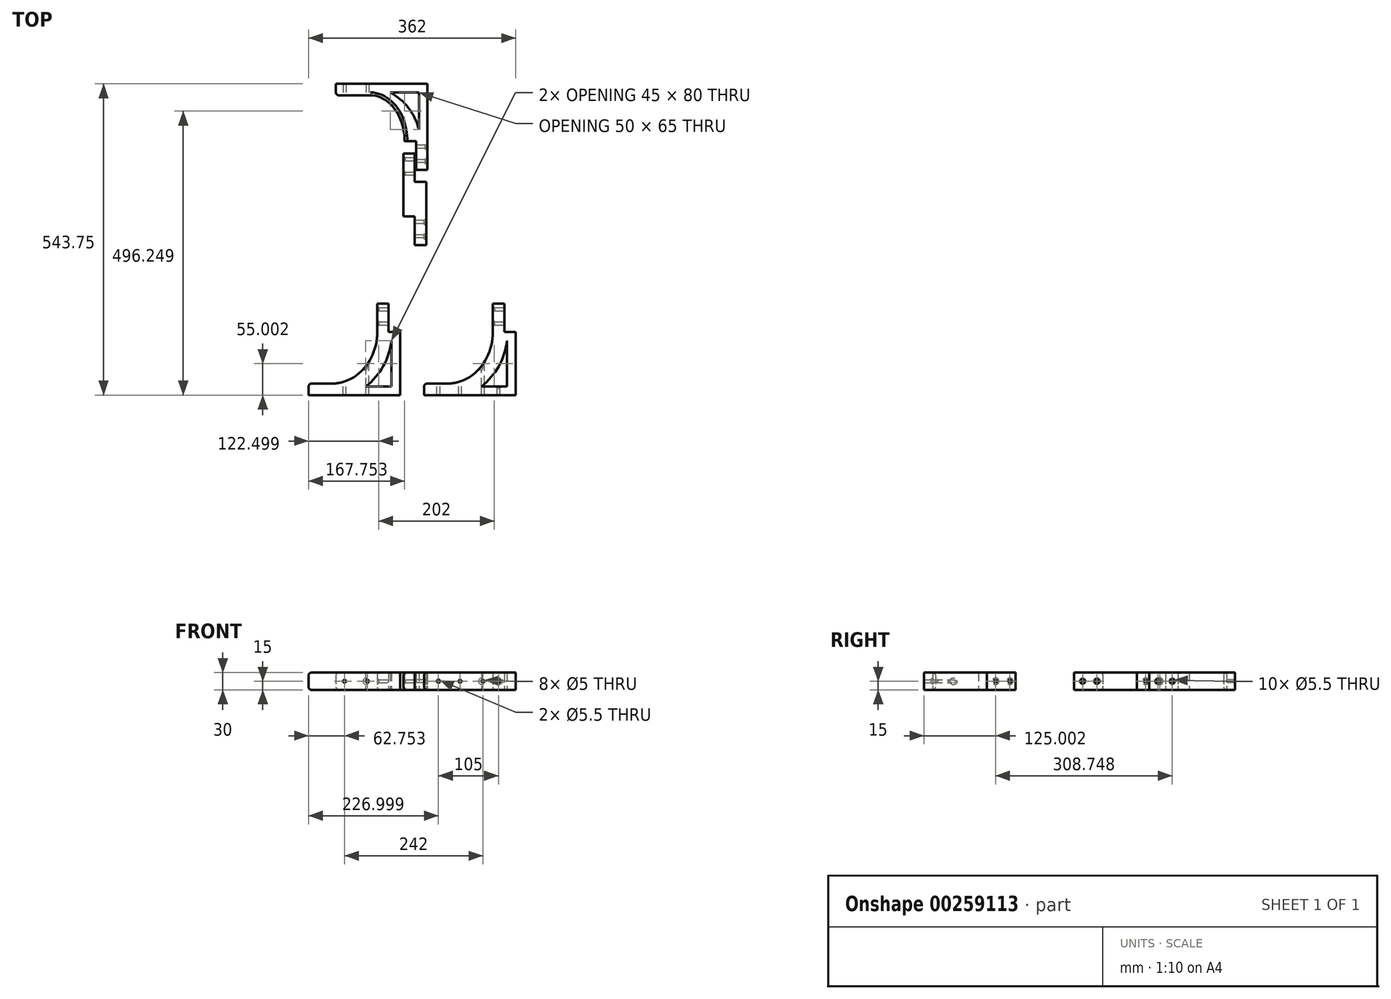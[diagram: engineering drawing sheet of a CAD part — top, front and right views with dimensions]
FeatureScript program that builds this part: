
annotation { "Feature Type Name" : "Feature", "Feature Type Description" : "" }
export const myFeature = defineFeature(function(context is Context, id is Id, definition is map)
    precondition{}
    {
        {
            var Q0;
            Q0=qCreatedBy(makeId("Top.planeOp"),FACE);
            var sketch = newSketch(context, id + "F0", { "sketchPlane" : qUnion([Q0])});
            skLineSegment(sketch, "E0", {"start": v(-102.14, 80.6) * mm, "end": v(57.86, 80.6) * mm});
            skLineSegment(sketch, "E1", {"start": v(57.86, 80.6) * mm, "end": v(57.86, -69.4) * mm});
            skLineSegment(sketch, "E2", {"start": v(57.86, -69.4) * mm, "end": v(37.86, -69.4) * mm});
            skLineSegment(sketch, "E3", {"start": v(17.86, -19.4) * mm, "end": v(17.86, 60.6) * mm});
            skLineSegment(sketch, "E4", {"start": v(17.86, 60.6) * mm, "end": v(-102.14, 60.6) * mm});
            skLineSegment(sketch, "E5", {"start": v(-102.14, 60.6) * mm, "end": v(-102.14, 80.6) * mm});
            skLineSegment(sketch, "E6", {"start": v(37.86, -69.4) * mm, "end": v(37.86, -19.4) * mm});
            skLineSegment(sketch, "E7", {"start": v(37.86, -19.4) * mm, "end": v(17.86, -19.4) * mm});
            skLineSegment(sketch, "E8.MirrorCS", {"start": v(-149.9, -443.15) * mm, "end": v(-149.9, -463.15) * mm});
            skLineSegment(sketch, "E9.MirrorCS", {"start": v(-9.9, -303.15) * mm, "end": v(-9.9, -353.15) * mm});
            skLineSegment(sketch, "E10.MirrorCS", {"start": v(10.1, -463.15) * mm, "end": v(10.1, -353.15) * mm});
            skLineSegment(sketch, "E11.MirrorCS", {"start": v(-149.9, -463.15) * mm, "end": v(10.1, -463.15) * mm});
            skLineSegment(sketch, "E12.MirrorCS", {"start": v(-29.9, -353.15) * mm, "end": v(-29.9, -353.15) * mm});
            skLineSegment(sketch, "E13.MirrorCS", {"start": v(-29.9, -353.15) * mm, "end": v(-109.9, -353.15) * mm, "construction": true});
            skLineSegment(sketch, "E14.MirrorCS", {"start": v(-29.9, -443.15) * mm, "end": v(-149.9, -443.15) * mm});
            skLineSegment(sketch, "E15.MirrorCS", {"start": v(-29.9, -313.15) * mm, "end": v(-29.9, -443.15) * mm});
            skLineSegment(sketch, "E16", {"start": v(-29.9, -313.15) * mm, "end": v(-29.9, -303.15) * mm});
            skLineSegment(sketch, "E17", {"start": v(-9.9, -303.15) * mm, "end": v(-29.9, -303.15) * mm});
            skLineSegment(sketch, "E18", {"start": v(-9.9, -353.15) * mm, "end": v(10.1, -353.15) * mm});
            skLineSegment(sketch, "E19", {"start": v(-109.9, -443.15) * mm, "end": v(-109.9, -353.15) * mm, "construction": true});
            skEllipticalArc(sketch, "E20", {});
            skLineSegment(sketch, "E21", {"start": v(-42.14, 60.6) * mm, "end": v(-42.14, -70.71) * mm, "construction": true});
            skLineSegment(sketch, "E22", {"start": v(17.86, -19.4) * mm, "end": v(-66.1, -19.4) * mm, "construction": true});
            skEllipticalArc(sketch, "E23", {});
            const initialGuessF0  = {"E20": [-0.10989091792114929, -0.3531483935056095, 0, -1, 0.09, 0.08, 0, 1.5707963267948966], "E23": [-0.04213666531701897, -0.019400740689241455, 1, 0, 0.06, 0.08, 6.283185307179586, 1.5707963267948966]};
            skSetInitialGuess(sketch, initialGuessF0);
            skSolve(sketch);
        }
        {
            var Q0;
            Q0 = qSketchRegion(id + "F0", true);
            extrude(context, id + "F1", {"entities" : qUnion([Q0]), "depth" : 30 * mm});
        }
        {
            var Q0;
            Q0=makeQuery(id+"F1.opExtrude","SWEPT_FACE",FACE,{"disambiguationData":[OSD([sQuery(id+"F0.wireOp",EDGE,"E4")])]});
            var sketch = newSketch(context, id + "F2", { "sketchPlane" : qUnion([Q0])});
            skLineSegment(sketch, "E24", {"start": v(-102.14, 15) * mm, "end": v(-102.14, 15) * mm});
            skCircle(sketch, "E25", {"center": v(-87.14, 15) * mm, "radius": 2.5 * mm});
            skCircle(sketch, "E26", {"center": v(-47.14, 15) * mm, "radius": 2.5 * mm});
            skSolve(sketch);
        }
        {
            var Q0;
            Q0 = qSketchRegion(id + "F2", true);
            extrude(context, id + "F3", {"entities" : qUnion([Q0]), "operationType" : NewBodyOperationType.REMOVE, "endBound" : BoundingType.THROUGH_ALL, "depth" : 500 * mm});
        }
        {
            var Q0;
            Q0 = qSketchRegion(id + "F2", true);
            var Q1;
            Q1 = qConstructionFilter(qBodyType(qCreatedBy(id + "F2" ,EDGE), BodyType.WIRE), ConstructionObject.NO);
            extrude(context, id + "F4", {"entities" : qUnion([Q0]), "operationType" : NewBodyOperationType.REMOVE, "surfaceEntities" : qUnion([Q1]), "endBound" : BoundingType.THROUGH_ALL, "oppositeDirection" : true, "depth" : 25 * mm});
        }
        {
            var Q0;
            Q0=makeQuery(id+"F1.opExtrude","SWEPT_FACE",FACE,{"disambiguationData":[OSD([sQuery(id+"F0.wireOp",EDGE,"E6")])]});
            var sketch = newSketch(context, id + "F5", { "sketchPlane" : qUnion([Q0])});
            skLineSegment(sketch, "E27", {"start": v(19.4, 15) * mm, "end": v(69.4, 15) * mm, "construction": true});
            skCircle(sketch, "E28", {"center": v(29.4, 15) * mm, "radius": 2.75 * mm});
            skCircle(sketch, "E29", {"center": v(54.4, 15) * mm, "radius": 2.75 * mm});
            skSolve(sketch);
        }
        {
            var Q0;
            Q0 = qSketchRegion(id + "F5", true);
            extrude(context, id + "F6", {"entities" : qUnion([Q0]), "operationType" : NewBodyOperationType.REMOVE, "endBound" : BoundingType.THROUGH_ALL, "oppositeDirection" : true, "depth" : 25 * mm});
        }
        {
            var Q0;
            Q0=makeQuery(id+"F1.opExtrude","SWEPT_FACE",FACE,{"disambiguationData":[OSD([sQuery(id+"F0.wireOp",EDGE,"E9.MirrorCS")])]});
            var sketch = newSketch(context, id + "F7", { "sketchPlane" : qUnion([Q0])});
            skLineSegment(sketch, "E30", {"start": v(-303.15, 15) * mm, "end": v(-353.15, 15) * mm, "construction": true});
            skCircle(sketch, "E31", {"center": v(-313.15, 15) * mm, "radius": 2.75 * mm});
            skCircle(sketch, "E32", {"center": v(-338.15, 15) * mm, "radius": 2.75 * mm});
            skSolve(sketch);
        }
        {
            var Q0;
            Q0 = qSketchRegion(id + "F7", true);
            extrude(context, id + "F8", {"entities" : qUnion([Q0]), "operationType" : NewBodyOperationType.REMOVE, "endBound" : BoundingType.THROUGH_ALL, "oppositeDirection" : true, "depth" : 25 * mm});
        }
        {
            var Q0;
            Q0=makeQuery(id+"F1.opExtrude","SWEPT_FACE",FACE,{"disambiguationData":[OSD([sQuery(id+"F0.wireOp",EDGE,"E15.MirrorCS"),sQuery(id+"F0.wireOp",EDGE,"E16")])]});
            var sketch = newSketch(context, id + "F9", { "sketchPlane" : qUnion([Q0])});
            skSolve(sketch);
        }
        {
            var Q0;
            Q0=makeQuery(id+"F9.imprint","IMPRINT",FACE,{"disambiguationData":[TD([[makeQuery(id+"F9.imprint","IMPRINT",EDGE,{"derivedFrom":makeQuery(id+"F8.boolean.opBoolean","INTERSECT",EDGE,{"derivedFrom":[makeQuery(id+"F1.opExtrude","SWEPT_FACE",FACE,{"disambiguationData":[OSD([sQuery(id+"F0.wireOp",EDGE,"E15.MirrorCS"),sQuery(id+"F0.wireOp",EDGE,"E16")])]}),makeQuery(id+"F8.opExtrude","SWEPT_FACE",FACE,{"disambiguationData":[OSD([sQuery(id+"F7.wireOp",EDGE,"E31")])]})]})}),1.0]])]});
            var Q1;
            Q1=makeQuery(id+"F9.imprint","IMPRINT",FACE,{"disambiguationData":[TD([[makeQuery(id+"F9.imprint","IMPRINT",EDGE,{"derivedFrom":makeQuery(id+"F8.boolean.opBoolean","INTERSECT",EDGE,{"derivedFrom":[makeQuery(id+"F1.opExtrude","SWEPT_FACE",FACE,{"disambiguationData":[OSD([sQuery(id+"F0.wireOp",EDGE,"E15.MirrorCS"),sQuery(id+"F0.wireOp",EDGE,"E16")])]}),makeQuery(id+"F8.opExtrude","SWEPT_FACE",FACE,{"disambiguationData":[OSD([sQuery(id+"F7.wireOp",EDGE,"E32")])]})]})}),1.0]])]});
            var Q2;
            Q2=makeQuery(id+"F9.imprint","IMPRINT",FACE,{"disambiguationData":[TD([[makeQuery(id+"F9.imprint","IMPRINT",EDGE,{"derivedFrom":sQuery(id+"F9.wireOp",EDGE,"272e9433-be63-4afe-911a-4138f05e95d2.0")}),-1.0]])]});
            var Q3;
            Q3=makeQuery(id+"F9.imprint","IMPRINT",FACE,{"disambiguationData":[TD([[makeQuery(id+"F9.imprint","IMPRINT",EDGE,{"derivedFrom":sQuery(id+"F9.wireOp",EDGE,"0a3e6cfc-d7aa-49eb-8218-c1783a06f407.0")}),-1.0]])]});
            extrude(context, id + "F10", {"entities" : qUnion([Q0, Q1, Q2, Q3]), "operationType" : NewBodyOperationType.REMOVE, "oppositeDirection" : true, "depth" : 4.5 * mm});
        }
        {
            var Q0;
            Q0=makeQuery(id+"F1.opExtrude","CAP_FACE",FACE,{"disambiguationData":[OSD([sQuery(id+"F0.wireOp",EDGE,"E8.MirrorCS"),sQuery(id+"F0.wireOp",EDGE,"E9.MirrorCS"),sQuery(id+"F0.wireOp",EDGE,"E10.MirrorCS"),sQuery(id+"F0.wireOp",EDGE,"E11.MirrorCS"),sQuery(id+"F0.wireOp",EDGE,"E14.MirrorCS"),sQuery(id+"F0.wireOp",EDGE,"E15.MirrorCS"),sQuery(id+"F0.wireOp",EDGE,"E16"),sQuery(id+"F0.wireOp",EDGE,"E17"),sQuery(id+"F0.wireOp",EDGE,"E18"),sQuery(id+"F0.wireOp",EDGE,"E20")])],"isStart":true});
            var sketch = newSketch(context, id + "F11", { "sketchPlane" : qUnion([Q0])});
            skLineSegment(sketch, "E33", {"start": v(-49.9, 448.15) * mm, "end": v(-4.9, 448.15) * mm});
            skLineSegment(sketch, "E34", {"start": v(-4.9, 448.15) * mm, "end": v(-4.9, 368.15) * mm});
            skArc(sketch, "E35", {"start": v(-4.9, 368.15) * mm, "mid": v(-19.44, 412.62) * mm, "end": v(-49.9, 448.15) * mm});
            skSolve(sketch);
        }
        {
            var Q0;
            Q0=makeQuery(id+"F11.imprint","IMPRINT",FACE,{"disambiguationData":[TD([[makeQuery(id+"F11.imprint","IMPRINT",EDGE,{"derivedFrom":sQuery(id+"F11.wireOp",EDGE,"E33")}),-1.0]])]});
            extrude(context, id + "F12", {"entities" : qUnion([Q0]), "operationType" : NewBodyOperationType.REMOVE, "endBound" : BoundingType.THROUGH_ALL, "oppositeDirection" : true, "depth" : 25 * mm});
        }
        {
            var Q0;
            Q0=makeQuery(id+"F1.opExtrude","CAP_FACE",FACE,{"disambiguationData":[OSD([sQuery(id+"F0.wireOp",EDGE,"E0"),sQuery(id+"F0.wireOp",EDGE,"E1"),sQuery(id+"F0.wireOp",EDGE,"E2"),sQuery(id+"F0.wireOp",EDGE,"E4"),sQuery(id+"F0.wireOp",EDGE,"E5"),sQuery(id+"F0.wireOp",EDGE,"E6"),sQuery(id+"F0.wireOp",EDGE,"E7"),sQuery(id+"F0.wireOp",EDGE,"E23")])],"isStart":true});
            var sketch = newSketch(context, id + "F13", { "sketchPlane" : qUnion([Q0])});
            skLineSegment(sketch, "E36", {"start": v(-7.14, -65.6) * mm, "end": v(42.86, -65.6) * mm});
            skLineSegment(sketch, "E37", {"start": v(42.86, -65.6) * mm, "end": v(42.86, -0.6) * mm});
            skArc(sketch, "E38", {"start": v(-7.14, -65.6) * mm, "mid": v(24.83, -38.46) * mm, "end": v(42.86, -0.6) * mm});
            skSolve(sketch);
        }
        {
            var Q0;
            Q0=makeQuery(id+"F13.imprint","IMPRINT",FACE,{"disambiguationData":[TD([[makeQuery(id+"F13.imprint","IMPRINT",EDGE,{"derivedFrom":sQuery(id+"F13.wireOp",EDGE,"E36")}),1.0]])]});
            extrude(context, id + "F14", {"entities" : qUnion([Q0]), "operationType" : NewBodyOperationType.REMOVE, "endBound" : BoundingType.THROUGH_ALL, "oppositeDirection" : true, "depth" : 25 * mm});
        }
        {
            var Q0;
            Q0=makeQuery(id+"F3.boolean.opBoolean","INTERSECT",EDGE,{"derivedFrom":[makeQuery(id+"F1.opExtrude","SWEPT_FACE",FACE,{"disambiguationData":[OSD([sQuery(id+"F0.wireOp",EDGE,"E20")])]}),makeQuery(id+"F3.opExtrude","SWEPT_FACE",FACE,{"disambiguationData":[OSD([sQuery(id+"F2.wireOp",EDGE,"E26")])]})]});
            var Q1;
            Q1=makeQuery(id+"F3.boolean.opBoolean","INTERSECT",EDGE,{"derivedFrom":[makeQuery(id+"F1.opExtrude","SWEPT_FACE",FACE,{"disambiguationData":[OSD([sQuery(id+"F0.wireOp",EDGE,"E14.MirrorCS")])]}),makeQuery(id+"F3.opExtrude","SWEPT_FACE",FACE,{"disambiguationData":[OSD([sQuery(id+"F2.wireOp",EDGE,"E25")])]})]});
            var Q2;
            Q2=makeQuery(id+"F3.boolean.opBoolean","INTERSECT",EDGE,{"derivedFrom":[makeQuery(id+"F1.opExtrude","SWEPT_FACE",FACE,{"disambiguationData":[OSD([sQuery(id+"F0.wireOp",EDGE,"E14.MirrorCS")])]}),makeQuery(id+"F3.opExtrude","SWEPT_FACE",FACE,{"disambiguationData":[OSD([sQuery(id+"F2.wireOp",EDGE,"E25")])]})]});
            var Q3;
            Q3=makeQuery(id+"F4.boolean.opBoolean","COPY",EDGE,{"derivedFrom":makeQuery(id+"F4.opExtrude","CAP_EDGE",EDGE,{"disambiguationData":[OSD([sQuery(id+"F2.wireOp",EDGE,"E25")])],"isStart":true})});
            var Q4;
            Q4=makeQuery(id+"F4.boolean.opBoolean","COPY",EDGE,{"derivedFrom":makeQuery(id+"F4.opExtrude","CAP_EDGE",EDGE,{"disambiguationData":[OSD([sQuery(id+"F2.wireOp",EDGE,"E26")])],"isStart":true})});
            chamfer(context, id + "F15", {"entities" : qUnion([Q0, Q1, Q2, Q3, Q4]), "width" : 3 * mm, "tangentPropagation" : true});
        }
        {
            var Q0;
            Q0=makeQuery(id+"F1.opExtrude","CAP_EDGE",EDGE,{"disambiguationData":[OSD([sQuery(id+"F0.wireOp",EDGE,"E14.MirrorCS")])],"isStart":true});
            var Q1;
            Q1=makeQuery(id+"F1.opExtrude","SWEPT_EDGE",EDGE,{"disambiguationData":[OSD([sQuery(id+"F0.wireOp",EDGE,"E8.MirrorCS"),sQuery(id+"F0.wireOp",EDGE,"E14.MirrorCS")])]});
            var Q2;
            Q2=makeQuery(id+"F1.opExtrude","CAP_EDGE",EDGE,{"disambiguationData":[OSD([sQuery(id+"F0.wireOp",EDGE,"E14.MirrorCS")])],"isStart":false});
            var Q3;
            Q3=makeQuery(id+"F1.opExtrude","CAP_EDGE",EDGE,{"disambiguationData":[OSD([sQuery(id+"F0.wireOp",EDGE,"E8.MirrorCS")])],"isStart":true});
            var Q4;
            Q4=makeQuery(id+"F1.opExtrude","CAP_EDGE",EDGE,{"disambiguationData":[OSD([sQuery(id+"F0.wireOp",EDGE,"E8.MirrorCS")])],"isStart":false});
            var Q5;
            Q5=makeQuery(id+"F1.opExtrude","CAP_EDGE",EDGE,{"disambiguationData":[OSD([sQuery(id+"F0.wireOp",EDGE,"E4")])],"isStart":true});
            var Q6;
            Q6=makeQuery(id+"F1.opExtrude","CAP_EDGE",EDGE,{"disambiguationData":[OSD([sQuery(id+"F0.wireOp",EDGE,"E5")])],"isStart":true});
            var Q7;
            Q7=makeQuery(id+"F1.opExtrude","SWEPT_EDGE",EDGE,{"disambiguationData":[OSD([sQuery(id+"F0.wireOp",EDGE,"E4"),sQuery(id+"F0.wireOp",EDGE,"E5")])]});
            var Q8;
            Q8=makeQuery(id+"F1.opExtrude","CAP_EDGE",EDGE,{"disambiguationData":[OSD([sQuery(id+"F0.wireOp",EDGE,"E5")])],"isStart":false});
            var Q9;
            Q9=makeQuery(id+"F1.opExtrude","CAP_EDGE",EDGE,{"disambiguationData":[OSD([sQuery(id+"F0.wireOp",EDGE,"E4")])],"isStart":false});
            fillet(context, id + "F16", {"entities" : qUnion([Q0, Q1, Q2, Q3, Q4, Q5, Q6, Q7, Q8, Q9]), "radius" : 5 * mm, "tangentPropagation" : true, "allowEdgeOverflow" : false});
        }
        {
            var Q0;
            Q0=makeQuery(id+"F8.boolean.opBoolean","INTERSECT",EDGE,{"derivedFrom":[makeQuery(id+"F1.opExtrude","SWEPT_FACE",FACE,{"disambiguationData":[OSD([sQuery(id+"F0.wireOp",EDGE,"E15.MirrorCS"),sQuery(id+"F0.wireOp",EDGE,"E16")])]}),makeQuery(id+"F8.opExtrude","SWEPT_FACE",FACE,{"disambiguationData":[OSD([sQuery(id+"F7.wireOp",EDGE,"E31")])]})]});
            var Q1;
            Q1=makeQuery(id+"F8.boolean.opBoolean","INTERSECT",EDGE,{"derivedFrom":[makeQuery(id+"F1.opExtrude","SWEPT_FACE",FACE,{"disambiguationData":[OSD([sQuery(id+"F0.wireOp",EDGE,"E15.MirrorCS"),sQuery(id+"F0.wireOp",EDGE,"E16")])]}),makeQuery(id+"F8.opExtrude","SWEPT_FACE",FACE,{"disambiguationData":[OSD([sQuery(id+"F7.wireOp",EDGE,"E32")])]})]});
            chamfer(context, id + "F17", {"entities" : qUnion([Q0, Q1]), "width" : 3 * mm, "tangentPropagation" : true});
        }
        {
            var Q0;
            Q0=makeQuery(id+"F1.opExtrude","SWEPT_FACE",FACE,{"disambiguationData":[OSD([sQuery(id+"F0.wireOp",EDGE,"E1")])]});
            var sketch = newSketch(context, id + "F18", { "sketchPlane" : qUnion([Q0])});
            skCircle(sketch, "E39.cCircle", {"center": v(-54.4, 15) * mm, "radius": 4.25 * mm, "construction": true});
            skLineSegment(sketch, "E39.0", {"start": v(-50.15, 17.45) * mm, "end": v(-50.15, 12.55) * mm});
            skLineSegment(sketch, "E39.1", {"start": v(-50.15, 12.55) * mm, "end": v(-54.4, 10.1) * mm});
            skLineSegment(sketch, "E39.2", {"start": v(-54.4, 10.1) * mm, "end": v(-58.65, 12.55) * mm});
            skLineSegment(sketch, "E39.3", {"start": v(-58.65, 12.55) * mm, "end": v(-58.65, 17.45) * mm});
            skLineSegment(sketch, "E39.4", {"start": v(-58.65, 17.45) * mm, "end": v(-54.4, 19.9) * mm});
            skLineSegment(sketch, "E39.5", {"start": v(-54.4, 19.9) * mm, "end": v(-50.15, 17.45) * mm});
            skPoint(sketch, "E39.0.midPoint", {"position": v(-50.15, 15) * mm});
            skCircle(sketch, "E40.cCircle", {"center": v(-29.4, 15) * mm, "radius": 4.25 * mm, "construction": true});
            skLineSegment(sketch, "E40.0", {"start": v(-25.15, 17.45) * mm, "end": v(-25.15, 12.55) * mm});
            skLineSegment(sketch, "E40.1", {"start": v(-25.15, 12.55) * mm, "end": v(-29.4, 10.1) * mm});
            skLineSegment(sketch, "E40.2", {"start": v(-29.4, 10.1) * mm, "end": v(-33.65, 12.55) * mm});
            skLineSegment(sketch, "E40.3", {"start": v(-33.65, 12.55) * mm, "end": v(-33.65, 17.45) * mm});
            skLineSegment(sketch, "E40.4", {"start": v(-33.65, 17.45) * mm, "end": v(-29.4, 19.9) * mm});
            skLineSegment(sketch, "E40.5", {"start": v(-29.4, 19.9) * mm, "end": v(-25.15, 17.45) * mm});
            skPoint(sketch, "E40.0.midPoint", {"position": v(-25.15, 15) * mm});
            skSolve(sketch);
        }
        {
            var Q0;
            Q0=makeQuery(id+"F18.imprint","IMPRINT",FACE,{"disambiguationData":[TD([[makeQuery(id+"F18.imprint","IMPRINT",EDGE,{"derivedFrom":sQuery(id+"F18.wireOp",EDGE,"E39.0")}),-1.0]])]});
            var Q1;
            Q1=makeQuery(id+"F18.imprint","IMPRINT",FACE,{"disambiguationData":[TD([[makeQuery(id+"F18.imprint","IMPRINT",EDGE,{"derivedFrom":sQuery(id+"F18.wireOp",EDGE,"E40.0")}),-1.0]])]});
            extrude(context, id + "F19", {"entities" : qUnion([Q0, Q1]), "operationType" : NewBodyOperationType.REMOVE, "oppositeDirection" : true, "depth" : 4 * mm});
        }
        {
            var Q0;
            Q0=qCreatedBy(makeId("Top.planeOp"),FACE);
            var sketch = newSketch(context, id + "F20", { "sketchPlane" : qUnion([Q0])});
            skLineSegment(sketch, "E41", {"start": v(15.8, -40.83) * mm, "end": v(15.8, -150.92) * mm});
            skLineSegment(sketch, "E42", {"start": v(15.8, -150.92) * mm, "end": v(35.8, -150.92) * mm});
            skLineSegment(sketch, "E43", {"start": v(35.8, -150.92) * mm, "end": v(35.8, -200.92) * mm});
            skLineSegment(sketch, "E44", {"start": v(35.8, -200.92) * mm, "end": v(55.8, -200.92) * mm});
            skLineSegment(sketch, "E45", {"start": v(55.8, -200.92) * mm, "end": v(55.8, -90.92) * mm});
            skLineSegment(sketch, "E46", {"start": v(55.8, -90.92) * mm, "end": v(35.8, -90.92) * mm});
            skLineSegment(sketch, "E47", {"start": v(35.8, -90.92) * mm, "end": v(35.8, -40.92) * mm});
            skLineSegment(sketch, "E48", {"start": v(35.8, -40.92) * mm, "end": v(15.8, -40.83) * mm});
            skSolve(sketch);
        }
        {
            var Q0;
            Q0 = qSketchRegion(id + "F20", true);
            extrude(context, id + "F21", {"entities" : qUnion([Q0]), "depth" : 30 * mm});
        }
        {
            var Q0;
            Q0=makeQuery(id+"F21.opExtrude","SWEPT_FACE",FACE,{"disambiguationData":[OSD([sQuery(id+"F20.wireOp",EDGE,"E43")])]});
            var sketch = newSketch(context, id + "F22", { "sketchPlane" : qUnion([Q0])});
            skLineSegment(sketch, "E49", {"start": v(150.92, 15) * mm, "end": v(200.92, 15) * mm, "construction": true});
            skCircle(sketch, "E50", {"center": v(160.92, 15) * mm, "radius": 2.75 * mm});
            skCircle(sketch, "E51", {"center": v(185.92, 15) * mm, "radius": 2.75 * mm});
            skSolve(sketch);
        }
        {
            var Q0;
            Q0 = qSketchRegion(id + "F22", true);
            extrude(context, id + "F23", {"entities" : qUnion([Q0]), "operationType" : NewBodyOperationType.REMOVE, "endBound" : BoundingType.THROUGH_ALL, "oppositeDirection" : true, "depth" : 25 * mm});
        }
        {
            var Q0;
            Q0=makeQuery(id+"F21.opExtrude","SWEPT_FACE",FACE,{"disambiguationData":[OSD([sQuery(id+"F20.wireOp",EDGE,"E45")])]});
            var sketch = newSketch(context, id + "F24", { "sketchPlane" : qUnion([Q0])});
            skCircle(sketch, "E52.cCircle", {"center": v(-160.92, 15) * mm, "radius": 4.25 * mm, "construction": true});
            skLineSegment(sketch, "E52.0", {"start": v(-156.67, 17.45) * mm, "end": v(-156.67, 12.55) * mm});
            skLineSegment(sketch, "E52.1", {"start": v(-156.67, 12.55) * mm, "end": v(-160.92, 10.1) * mm});
            skLineSegment(sketch, "E52.2", {"start": v(-160.92, 10.1) * mm, "end": v(-165.17, 12.55) * mm});
            skLineSegment(sketch, "E52.3", {"start": v(-165.17, 12.55) * mm, "end": v(-165.17, 17.45) * mm});
            skLineSegment(sketch, "E52.4", {"start": v(-165.17, 17.45) * mm, "end": v(-160.92, 19.9) * mm});
            skLineSegment(sketch, "E52.5", {"start": v(-160.92, 19.9) * mm, "end": v(-156.67, 17.45) * mm});
            skPoint(sketch, "E52.0.midPoint", {"position": v(-156.67, 15) * mm});
            skCircle(sketch, "E53.cCircle", {"center": v(-185.92, 15) * mm, "radius": 4.25 * mm, "construction": true});
            skLineSegment(sketch, "E53.0", {"start": v(-181.67, 17.45) * mm, "end": v(-181.67, 12.55) * mm});
            skLineSegment(sketch, "E53.1", {"start": v(-181.67, 12.55) * mm, "end": v(-185.92, 10.1) * mm});
            skLineSegment(sketch, "E53.2", {"start": v(-185.92, 10.1) * mm, "end": v(-190.17, 12.55) * mm});
            skLineSegment(sketch, "E53.3", {"start": v(-190.17, 12.55) * mm, "end": v(-190.17, 17.45) * mm});
            skLineSegment(sketch, "E53.4", {"start": v(-190.17, 17.45) * mm, "end": v(-185.92, 19.9) * mm});
            skLineSegment(sketch, "E53.5", {"start": v(-185.92, 19.9) * mm, "end": v(-181.67, 17.45) * mm});
            skPoint(sketch, "E53.0.midPoint", {"position": v(-181.67, 15) * mm});
            skSolve(sketch);
        }
        {
            var Q0;
            Q0 = qSketchRegion(id + "F24", true);
            extrude(context, id + "F25", {"entities" : qUnion([Q0]), "operationType" : NewBodyOperationType.REMOVE, "oppositeDirection" : true, "depth" : 4 * mm});
        }
        {
            var Q0;
            Q0=makeQuery(id+"F21.opExtrude","SWEPT_FACE",FACE,{"disambiguationData":[OSD([sQuery(id+"F20.wireOp",EDGE,"E47")])]});
            var sketch = newSketch(context, id + "F26", { "sketchPlane" : qUnion([Q0])});
            skLineSegment(sketch, "E54", {"start": v(-90.92, 15) * mm, "end": v(-40.92, 15) * mm, "construction": true});
            skCircle(sketch, "E55", {"center": v(-75.92, 15) * mm, "radius": 2.75 * mm});
            skCircle(sketch, "E56", {"center": v(-50.92, 15) * mm, "radius": 2.75 * mm});
            skSolve(sketch);
        }
        {
            var Q0;
            Q0 = qSketchRegion(id + "F26", true);
            extrude(context, id + "F27", {"entities" : qUnion([Q0]), "operationType" : NewBodyOperationType.REMOVE, "endBound" : BoundingType.THROUGH_ALL, "oppositeDirection" : true, "depth" : 25 * mm});
        }
        {
            var Q0;
            Q0=makeQuery(id+"F27.boolean.opBoolean","INTERSECT",EDGE,{"derivedFrom":[makeQuery(id+"F21.opExtrude","SWEPT_FACE",FACE,{"disambiguationData":[OSD([sQuery(id+"F20.wireOp",EDGE,"E41")])]}),makeQuery(id+"F27.opExtrude","SWEPT_FACE",FACE,{"disambiguationData":[OSD([sQuery(id+"F26.wireOp",EDGE,"E56")])]})]});
            var Q1;
            Q1=makeQuery(id+"F27.boolean.opBoolean","INTERSECT",EDGE,{"derivedFrom":[makeQuery(id+"F21.opExtrude","SWEPT_FACE",FACE,{"disambiguationData":[OSD([sQuery(id+"F20.wireOp",EDGE,"E41")])]}),makeQuery(id+"F27.opExtrude","SWEPT_FACE",FACE,{"disambiguationData":[OSD([sQuery(id+"F26.wireOp",EDGE,"E55")])]})]});
            chamfer(context, id + "F28", {"entities" : qUnion([Q0, Q1]), "width" : 3 * mm, "tangentPropagation" : true});
        }
        {
            var Q0;
            Q0=makeQuery(id+"F21.opExtrude","CAP_EDGE",EDGE,{"disambiguationData":[OSD([sQuery(id+"F20.wireOp",EDGE,"E41")])],"isStart":false});
            var Q1;
            Q1=makeQuery(id+"F21.opExtrude","CAP_EDGE",EDGE,{"disambiguationData":[OSD([sQuery(id+"F20.wireOp",EDGE,"E41")])],"isStart":true});
            fillet(context, id + "F29", {"entities" : qUnion([Q0, Q1]), "radius" : 5 * mm, "tangentPropagation" : true, "allowEdgeOverflow" : false});
        }
        {
            var Q0;
            Q0=makeQuery(id+"F1.opExtrude","SWEPT_BODY",BODY,{"disambiguationData":[OSD([sQuery(id+"F0.wireOp",EDGE,"E8.MirrorCS"),sQuery(id+"F0.wireOp",EDGE,"E9.MirrorCS"),sQuery(id+"F0.wireOp",EDGE,"E10.MirrorCS"),sQuery(id+"F0.wireOp",EDGE,"E11.MirrorCS"),sQuery(id+"F0.wireOp",EDGE,"E14.MirrorCS"),sQuery(id+"F0.wireOp",EDGE,"E15.MirrorCS"),sQuery(id+"F0.wireOp",EDGE,"E16"),sQuery(id+"F0.wireOp",EDGE,"E17"),sQuery(id+"F0.wireOp",EDGE,"E18"),sQuery(id+"F0.wireOp",EDGE,"E20")])]});
            transform(context, id + "F30", {"entities" : qUnion([Q0]), "transformType" : TransformType.TRANSLATION_3D, "dx" : 202 * mm, "dy" : 0 * mm, "dz" : 0 * mm, "makeCopy" : true});
        }
        {
            var Q0;
            Q0=makeQuery(id+"F30.opPattern","COPY",FACE,{"derivedFrom":makeQuery(id+"F1.opExtrude","SWEPT_FACE",FACE,{"disambiguationData":[OSD([sQuery(id+"F0.wireOp",EDGE,"E14.MirrorCS")])]}),"instanceName":"1"});
            var sketch = newSketch(context, id + "F31", { "sketchPlane" : qUnion([Q0])});
            skLineSegment(sketch, "E57", {"start": v(-57.1, 15) * mm, "end": v(-92.1, 15) * mm, "construction": true});
            skCircle(sketch, "E58", {"center": v(-182.1, 15) * mm, "radius": 2.75 * mm});
            skCircle(sketch, "E59", {"center": v(-77.1, 15) * mm, "radius": 2.75 * mm});
            skSolve(sketch);
        }
        {
            var Q0;
            Q0 = qSketchRegion(id + "F31", true);
            var Q1;
            Q1=makeQuery(id+"F30.opPattern","COPY",FACE,{"derivedFrom":makeQuery(id+"F1.opExtrude","SWEPT_FACE",FACE,{"disambiguationData":[OSD([sQuery(id+"F0.wireOp",EDGE,"E11.MirrorCS")])]}),"instanceName":"1"});
            extrude(context, id + "F32", {"entities" : qUnion([Q0]), "operationType" : NewBodyOperationType.REMOVE, "endBound" : BoundingType.THROUGH_ALL, "oppositeDirection" : true, "endBoundEntityFace" : qUnion([Q1]), "depth" : 25 * mm});
        }
        {
            var Q0;
            Q0=makeQuery(id+"F32.boolean.opBoolean","COPY",EDGE,{"derivedFrom":makeQuery(id+"F32.opExtrude","CAP_EDGE",EDGE,{"disambiguationData":[OSD([sQuery(id+"F31.wireOp",EDGE,"E59")])],"isStart":true})});
            var Q1;
            Q1=makeQuery(id+"F32.boolean.opBoolean","INTERSECT",EDGE,{"derivedFrom":[makeQuery(id+"F30.opPattern","COPY",FACE,{"derivedFrom":makeQuery(id+"F12.boolean.opBoolean","COPY",FACE,{"derivedFrom":makeQuery(id+"F12.opExtrude","SWEPT_FACE",FACE,{"disambiguationData":[OSD([sQuery(id+"F11.wireOp",EDGE,"E33")])]})}),"instanceName":"1"}),makeQuery(id+"F32.opExtrude","SWEPT_FACE",FACE,{"disambiguationData":[OSD([sQuery(id+"F31.wireOp",EDGE,"E58")])]})]});
            chamfer(context, id + "F33", {"entities" : qUnion([Q0, Q1]), "width" : 3 * mm, "tangentPropagation" : true});
        }
    });
